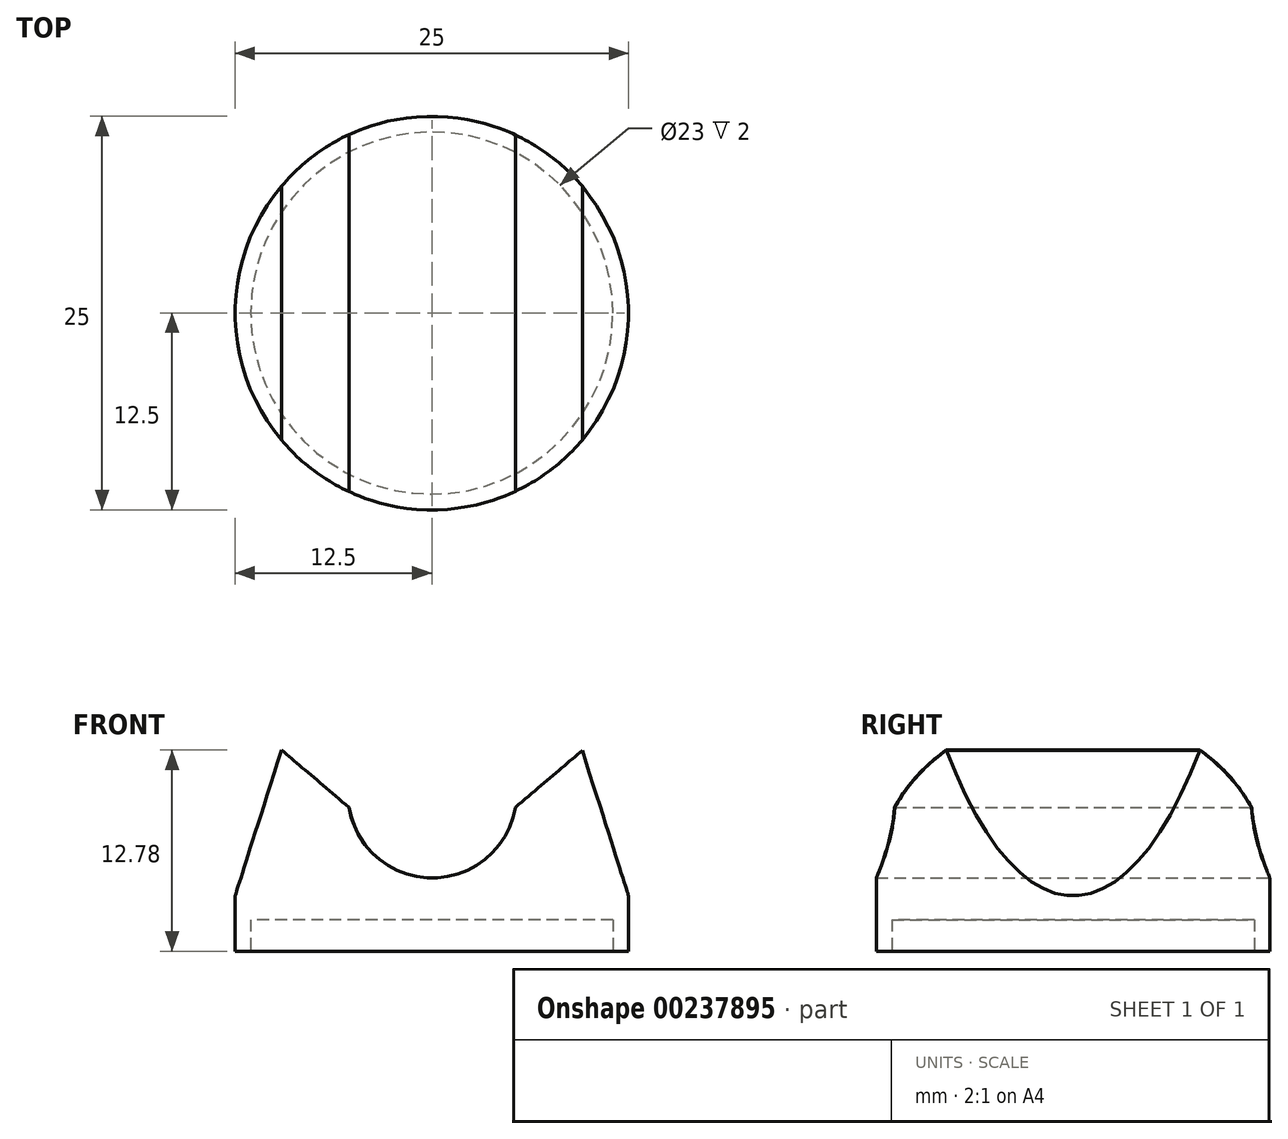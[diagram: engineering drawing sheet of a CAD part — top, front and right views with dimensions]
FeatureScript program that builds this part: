
annotation { "Feature Type Name" : "Feature", "Feature Type Description" : "" }
export const myFeature = defineFeature(function(context is Context, id is Id, definition is map)
    precondition{}
    {
        {
            var Q0;
            Q0=qCreatedBy(makeId("Top.planeOp"),FACE);
            var sketch = newSketch(context, id + "F0", { "sketchPlane" : qUnion([Q0])});
            skCircle(sketch, "E0", {"center": v(0, 0) * mm, "radius": 12.5 * mm});
            skSolve(sketch);
        }
        {
            var Q0;
            Q0=makeQuery(id+"F0.imprint","IMPRINT",FACE,{"disambiguationData":[TD([[makeQuery(id+"F0.imprint","IMPRINT",EDGE,{"derivedFrom":sQuery(id+"F0.wireOp",EDGE,"E0")}),1.0]])]});
            extrude(context, id + "F1", {"entities" : qUnion([Q0]), "depth" : 15 * mm});
        }
        {
            var Q0;
            Q0=qCreatedBy(makeId("Front.planeOp"),FACE);
            var sketch = newSketch(context, id + "F2", { "sketchPlane" : qUnion([Q0])});
            skCircle(sketch, "E1", {"center": v(0.02, 10) * mm, "radius": 5.35 * mm});
            skSolve(sketch);
        }
        {
            var Q0;
            Q0 = qSketchRegion(id + "F2", true);
            extrude(context, id + "F3", {"entities" : qUnion([Q0]), "operationType" : NewBodyOperationType.REMOVE, "endBound" : BoundingType.SYMMETRIC, "depth" : 39.4 * mm});
        }
        {
            var Q0;
            Q0=qCreatedBy(makeId("Top.planeOp"),FACE);
            var sketch = newSketch(context, id + "F4", { "sketchPlane" : qUnion([Q0])});
            skCircle(sketch, "E2", {"center": v(0, 0) * mm, "radius": 11.5 * mm});
            skSolve(sketch);
        }
        {
            var Q0;
            Q0 = qSketchRegion(id + "F4", true);
            extrude(context, id + "F5", {"entities" : qUnion([Q0]), "operationType" : NewBodyOperationType.REMOVE, "depth" : 2 * mm});
        }
        {
            var Q0;
            Q0=makeQuery(id+"F3.boolean.opBoolean","INTERSECT",EDGE,{"disambiguationData":[OD(0.0)],"derivedFrom":[makeQuery(id+"F1.opExtrude","CAP_FACE",FACE,{"disambiguationData":[OSD([sQuery(id+"F0.wireOp",EDGE,"E0")])],"isStart":false}),makeQuery(id+"F3.opExtrude","SWEPT_FACE",FACE,{"disambiguationData":[OSD([sQuery(id+"F2.wireOp",EDGE,"E1")])]})]});
            var Q1;
            Q1=makeQuery(id+"F3.boolean.opBoolean","INTERSECT",EDGE,{"disambiguationData":[OD(1.0)],"derivedFrom":[makeQuery(id+"F1.opExtrude","CAP_FACE",FACE,{"disambiguationData":[OSD([sQuery(id+"F0.wireOp",EDGE,"E0")])],"isStart":false}),makeQuery(id+"F3.opExtrude","SWEPT_FACE",FACE,{"disambiguationData":[OSD([sQuery(id+"F2.wireOp",EDGE,"E1")])]})]});
            chamfer(context, id + "F6", {"entities" : qUnion([Q0, Q1]), "width" : 7 * mm, "tangentPropagation" : true});
        }
        {
            var Q0;
            Q0=qCreatedBy(makeId("Front.planeOp"),FACE);
            var sketch = newSketch(context, id + "F7", { "sketchPlane" : qUnion([Q0])});
            skLineSegment(sketch, "E3", {"start": v(7.12, 20.45) * mm, "end": v(14.58, -3.04) * mm});
            skLineSegment(sketch, "E4", {"start": v(14.58, -3.04) * mm, "end": v(22.1, 20.64) * mm});
            skLineSegment(sketch, "E5", {"start": v(22.1, 20.64) * mm, "end": v(7.12, 20.45) * mm});
            skLineSegment(sketch, "E6.MirrorCS", {"start": v(-7.12, 20.45) * mm, "end": v(-14.58, -3.04) * mm});
            skLineSegment(sketch, "E7.MirrorCS", {"start": v(-14.58, -3.04) * mm, "end": v(-22.1, 20.64) * mm});
            skLineSegment(sketch, "E8.MirrorCS", {"start": v(-22.1, 20.64) * mm, "end": v(-7.12, 20.45) * mm});
            skSolve(sketch);
        }
        {
            var Q0;
            Q0=makeQuery(id+"F7.imprint","IMPRINT",FACE,{"disambiguationData":[TD([[makeQuery(id+"F7.imprint","IMPRINT",EDGE,{"derivedFrom":sQuery(id+"F7.wireOp",EDGE,"E3")}),1.0]])]});
            var Q1;
            Q1=makeQuery(id+"F7.imprint","IMPRINT",FACE,{"disambiguationData":[TD([[makeQuery(id+"F7.imprint","IMPRINT",EDGE,{"derivedFrom":sQuery(id+"F7.wireOp",EDGE,"E3")}),1.0]])]});
            var Q2;
            Q2=makeQuery(id+"F7.imprint","IMPRINT",FACE,{"disambiguationData":[TD([[makeQuery(id+"F7.imprint","IMPRINT",EDGE,{"derivedFrom":sQuery(id+"F7.wireOp",EDGE,"E6.MirrorCS")}),-1.0]])]});
            extrude(context, id + "F8", {"entities" : qUnion([Q0, Q1, Q2]), "operationType" : NewBodyOperationType.REMOVE, "endBound" : BoundingType.SYMMETRIC, "depth" : 82 * mm});
        }
    });
